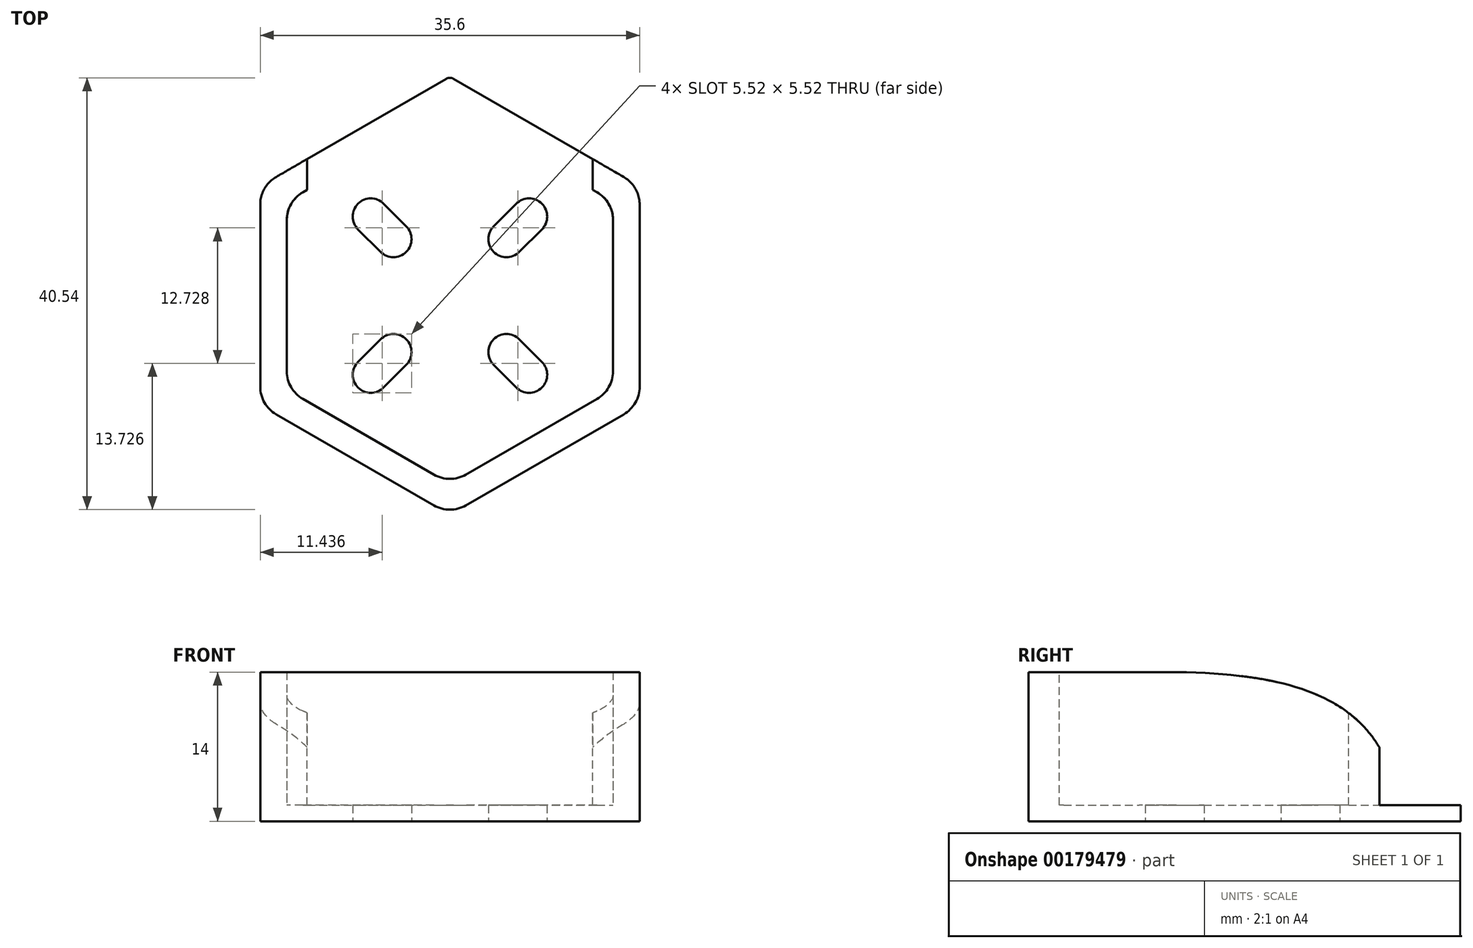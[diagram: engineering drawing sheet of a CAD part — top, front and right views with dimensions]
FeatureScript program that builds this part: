
annotation { "Feature Type Name" : "Feature", "Feature Type Description" : "" }
export const myFeature = defineFeature(function(context is Context, id is Id, definition is map)
    precondition{}
    {
        {
            var Q0;
            Q0=qCreatedBy(makeId("Top.planeOp"),FACE);
            var sketch = newSketch(context, id + "F0", { "sketchPlane" : qUnion([Q0])});
            skPoint(sketch, "E0", {"position": v(0, 0) * mm});
            skLineSegment(sketch, "E1", {"start": v(-20.56, -20.56) * mm, "end": v(20.56, 20.56) * mm, "construction": true});
            skLineSegment(sketch, "E2", {"start": v(-19.47, 19.47) * mm, "end": v(19.47, -19.47) * mm, "construction": true});
            skArc(sketch, "E3", {"start": v(-6.22, 8.63) * mm, "mid": v(-8.63, 8.63) * mm, "end": v(-8.63, 6.22) * mm});
            skArc(sketch, "E4", {"start": v(-6.5, 4.1) * mm, "mid": v(-4.1, 4.1) * mm, "end": v(-4.1, 6.5) * mm});
            skLineSegment(sketch, "E5", {"start": v(-6.22, 8.63) * mm, "end": v(-4.1, 6.5) * mm});
            skLineSegment(sketch, "E6", {"start": v(-8.63, 6.22) * mm, "end": v(-6.5, 4.1) * mm});
            skLineSegment(sketch, "E7.MirrorCS", {"start": v(-8.63, -6.22) * mm, "end": v(-6.5, -4.1) * mm});
            skArc(sketch, "E8.MirrorCS", {"start": v(-6.22, -8.63) * mm, "mid": v(-8.63, -8.63) * mm, "end": v(-8.63, -6.22) * mm});
            skArc(sketch, "E9.MirrorCS", {"start": v(-6.5, -4.1) * mm, "mid": v(-4.1, -4.1) * mm, "end": v(-4.1, -6.5) * mm});
            skLineSegment(sketch, "E10.MirrorCS", {"start": v(-6.22, -8.63) * mm, "end": v(-4.1, -6.5) * mm});
            skLineSegment(sketch, "E11.MirrorCS", {"start": v(6.22, -8.63) * mm, "end": v(4.1, -6.5) * mm});
            skLineSegment(sketch, "E12.MirrorCS", {"start": v(8.63, -6.22) * mm, "end": v(6.5, -4.1) * mm});
            skLineSegment(sketch, "E13.MirrorCS", {"start": v(6.22, 8.63) * mm, "end": v(4.1, 6.5) * mm});
            skArc(sketch, "E14.MirrorCS", {"start": v(6.5, -4.1) * mm, "mid": v(4.1, -4.1) * mm, "end": v(4.1, -6.5) * mm});
            skLineSegment(sketch, "E15.MirrorCS", {"start": v(8.63, 6.22) * mm, "end": v(6.5, 4.1) * mm});
            skArc(sketch, "E16.MirrorCS", {"start": v(6.22, -8.63) * mm, "mid": v(8.63, -8.63) * mm, "end": v(8.63, -6.22) * mm});
            skArc(sketch, "E17.MirrorCS", {"start": v(6.22, 8.63) * mm, "mid": v(8.63, 8.63) * mm, "end": v(8.63, 6.22) * mm});
            skArc(sketch, "E18.MirrorCS", {"start": v(6.5, 4.1) * mm, "mid": v(4.1, 4.1) * mm, "end": v(4.1, 6.5) * mm});
            skCircle(sketch, "E19.cCircle", {"center": v(0, 0) * mm, "radius": 15.3 * mm, "construction": true});
            skLineSegment(sketch, "E19.0", {"start": v(15.3, -8.83) * mm, "end": v(0, -17.67) * mm});
            skLineSegment(sketch, "E19.1", {"start": v(0, -17.67) * mm, "end": v(-15.3, -8.83) * mm});
            skLineSegment(sketch, "E19.2", {"start": v(-15.3, -8.83) * mm, "end": v(-15.3, 8.83) * mm});
            skLineSegment(sketch, "E19.3", {"start": v(-15.3, 8.83) * mm, "end": v(0, 17.67) * mm});
            skLineSegment(sketch, "E19.4", {"start": v(0, 17.67) * mm, "end": v(15.3, 8.83) * mm});
            skLineSegment(sketch, "E19.5", {"start": v(15.3, 8.83) * mm, "end": v(15.3, -8.83) * mm});
            skPoint(sketch, "E19.0.midPoint", {"position": v(7.65, -13.25) * mm});
            skLineSegment(sketch, "E20.0", {"start": v(-17.8, -10.28) * mm, "end": v(-17.8, 10.28) * mm});
            skLineSegment(sketch, "E20.1", {"start": v(0, 20.55) * mm, "end": v(17.8, 10.28) * mm});
            skLineSegment(sketch, "E20.2", {"start": v(17.8, 10.28) * mm, "end": v(17.8, -10.28) * mm});
            skLineSegment(sketch, "E20.3", {"start": v(-17.8, 10.28) * mm, "end": v(0, 20.55) * mm});
            skLineSegment(sketch, "E20.4", {"start": v(17.8, -10.28) * mm, "end": v(0, -20.55) * mm});
            skLineSegment(sketch, "E20.5", {"start": v(0, -20.55) * mm, "end": v(-17.8, -10.28) * mm});
            skSolve(sketch);
        }
        {
            var Q0;
            Q0=makeQuery(id+"F0.imprint","IMPRINT",FACE,{"disambiguationData":[TD([[makeQuery(id+"F0.imprint","IMPRINT",EDGE,{"derivedFrom":sQuery(id+"F0.wireOp",EDGE,"E3")}),-1.0]])]});
            extrude(context, id + "F1", {"entities" : qUnion([Q0]), "depth" : 1.5 * mm});
        }
        {
            var Q0;
            Q0=makeQuery(id+"F0.imprint","IMPRINT",FACE,{"disambiguationData":[TD([[makeQuery(id+"F0.imprint","IMPRINT",EDGE,{"derivedFrom":sQuery(id+"F0.wireOp",EDGE,"E19.0")}),1.0]])]});
            extrude(context, id + "F2", {"entities" : qUnion([Q0]), "operationType" : NewBodyOperationType.ADD, "depth" : 14 * mm, "offsetDistance" : 25 * mm});
        }
        {
            var Q0;
            Q0=qCreatedBy(makeId("Front.planeOp"),FACE);
            cPlane(context, id + "F3", {"entities" : qUnion([Q0]), "cplaneType" : CPlaneType.OFFSET, "offset" : 25 * mm, "oppositeDirection" : true, "width" : 150 * mm, "height" : 150 * mm});
        }
        {
            var Q0;
            Q0=qCreatedBy(id+"F3.planeOp",FACE);
            var sketch = newSketch(context, id + "F4", { "sketchPlane" : qUnion([Q0])});
            skLineSegment(sketch, "E21.bottom", {"start": v(-13.4, 1.5) * mm, "end": v(13.4, 1.5) * mm});
            skLineSegment(sketch, "E21.top", {"start": v(-13.4, 17.25) * mm, "end": v(13.4, 17.25) * mm});
            skLineSegment(sketch, "E21.left", {"start": v(-13.4, 1.5) * mm, "end": v(-13.4, 17.25) * mm});
            skLineSegment(sketch, "E21.right", {"start": v(13.4, 1.5) * mm, "end": v(13.4, 17.25) * mm});
            skPoint(sketch, "E21.middle", {"position": v(0, 9.37) * mm});
            skSolve(sketch);
        }
        {
            var Q0;
            Q0=makeQuery(id+"F4.imprint","IMPRINT",FACE,{"disambiguationData":[TD([[makeQuery(id+"F4.imprint","IMPRINT",EDGE,{"derivedFrom":sQuery(id+"F4.wireOp",EDGE,"E21.bottom")}),1.0]])]});
            extrude(context, id + "F5", {"entities" : qUnion([Q0]), "operationType" : NewBodyOperationType.REMOVE, "depth" : 26 * mm});
        }
        {
            var Q0;
            Q0=makeQuery(id+"F2.opExtrude","SWEPT_EDGE",EDGE,{"disambiguationData":[OSD([sQuery(id+"F0.wireOp",EDGE,"E20.1"),sQuery(id+"F0.wireOp",EDGE,"E20.2")])]});
            var Q1;
            Q1=makeQuery(id+"F2.opExtrude","SWEPT_EDGE",EDGE,{"disambiguationData":[OSD([sQuery(id+"F0.wireOp",EDGE,"E20.0"),sQuery(id+"F0.wireOp",EDGE,"E20.3")])]});
            var Q2;
            Q2=makeQuery(id+"F2.opExtrude","SWEPT_EDGE",EDGE,{"disambiguationData":[OSD([sQuery(id+"F0.wireOp",EDGE,"E20.0"),sQuery(id+"F0.wireOp",EDGE,"E20.5")])]});
            var Q3;
            Q3=makeQuery(id+"F2.opExtrude","SWEPT_EDGE",EDGE,{"disambiguationData":[OSD([sQuery(id+"F0.wireOp",EDGE,"E20.4"),sQuery(id+"F0.wireOp",EDGE,"E20.5")])]});
            var Q4;
            Q4=makeQuery(id+"F2.opExtrude","SWEPT_EDGE",EDGE,{"disambiguationData":[OSD([sQuery(id+"F0.wireOp",EDGE,"E20.2"),sQuery(id+"F0.wireOp",EDGE,"E20.4")])]});
            var Q5;
            Q5=makeQuery(id+"F2.opExtrude","SWEPT_EDGE",EDGE,{"disambiguationData":[OSD([sQuery(id+"F0.wireOp",EDGE,"E19.4"),sQuery(id+"F0.wireOp",EDGE,"E19.5")])]});
            var Q6;
            Q6=makeQuery(id+"F2.opExtrude","SWEPT_EDGE",EDGE,{"disambiguationData":[OSD([sQuery(id+"F0.wireOp",EDGE,"E19.0"),sQuery(id+"F0.wireOp",EDGE,"E19.5")])]});
            var Q7;
            Q7=makeQuery(id+"F2.opExtrude","SWEPT_EDGE",EDGE,{"disambiguationData":[OSD([sQuery(id+"F0.wireOp",EDGE,"E19.0"),sQuery(id+"F0.wireOp",EDGE,"E19.1")])]});
            var Q8;
            Q8=makeQuery(id+"F2.opExtrude","SWEPT_EDGE",EDGE,{"disambiguationData":[OSD([sQuery(id+"F0.wireOp",EDGE,"E19.1"),sQuery(id+"F0.wireOp",EDGE,"E19.2")])]});
            var Q9;
            Q9=makeQuery(id+"F2.opExtrude","SWEPT_EDGE",EDGE,{"disambiguationData":[OSD([sQuery(id+"F0.wireOp",EDGE,"E19.2"),sQuery(id+"F0.wireOp",EDGE,"E19.3")])]});
            fillet(context, id + "F6", {"entities" : qUnion([Q0, Q1, Q2, Q3, Q4, Q5, Q6, Q7, Q8, Q9]), "radius" : 3 * mm, "tangentPropagation" : true, "allowEdgeOverflow" : false});
        }
        {
            var Q0;
            Q0=makeQuery(id+"F1.opExtrude","CAP_EDGE",EDGE,{"disambiguationData":[OSD([sQuery(id+"F0.wireOp",EDGE,"E19.3")])],"isStart":false});
            var Q1;
            Q1=makeQuery(id+"F2.opExtrude","SWEPT_EDGE",EDGE,{"disambiguationData":[OSD([sQuery(id+"F0.wireOp",EDGE,"E20.1"),sQuery(id+"F0.wireOp",EDGE,"E20.3")])]});
            fillet(context, id + "F7", {"entities" : qUnion([Q0, Q1]), "radius" : 0.7 * mm, "tangentPropagation" : true, "allowEdgeOverflow" : false});
        }
        {
            var Q0;
            Q0=qCreatedBy(makeId("Right.planeOp"),FACE);
            var sketch = newSketch(context, id + "F8", { "sketchPlane" : qUnion([Q0])});
            skPoint(sketch, "E22.0", {"position": v(-7.1, 14) * mm});
            skFitSpline(sketch, "E23", {"points": [v(-7.1, 14) * mm, v(13.07, 6.5) * mm], "startDerivative": vector(34.6, 0) * mm, "endDerivative": vector(8.36, -15.26) * mm});
            skLineSegment(sketch, "E24", {"start": v(-7.1, 14) * mm, "end": v(13.07, 14) * mm});
            skLineSegment(sketch, "E25", {"start": v(13.07, 14) * mm, "end": v(13.07, 6.5) * mm});
            skLineSegment(sketch, "E26.0", {"start": v(20.35, 1.5) * mm, "end": v(12.82, 1.5) * mm});
            skSolve(sketch);
        }
        {
            var Q0;
            Q0=makeQuery(id+"F8.imprint","IMPRINT",FACE,{"disambiguationData":[TD([[makeQuery(id+"F8.imprint","IMPRINT",EDGE,{"derivedFrom":sQuery(id+"F8.wireOp",EDGE,"E23")}),1.0]])]});
            extrude(context, id + "F9", {"entities" : qUnion([Q0]), "operationType" : NewBodyOperationType.REMOVE, "endBound" : BoundingType.SYMMETRIC, "oppositeDirection" : true, "depth" : 37.6 * mm, "offsetDistance" : 25 * mm});
        }
    });
